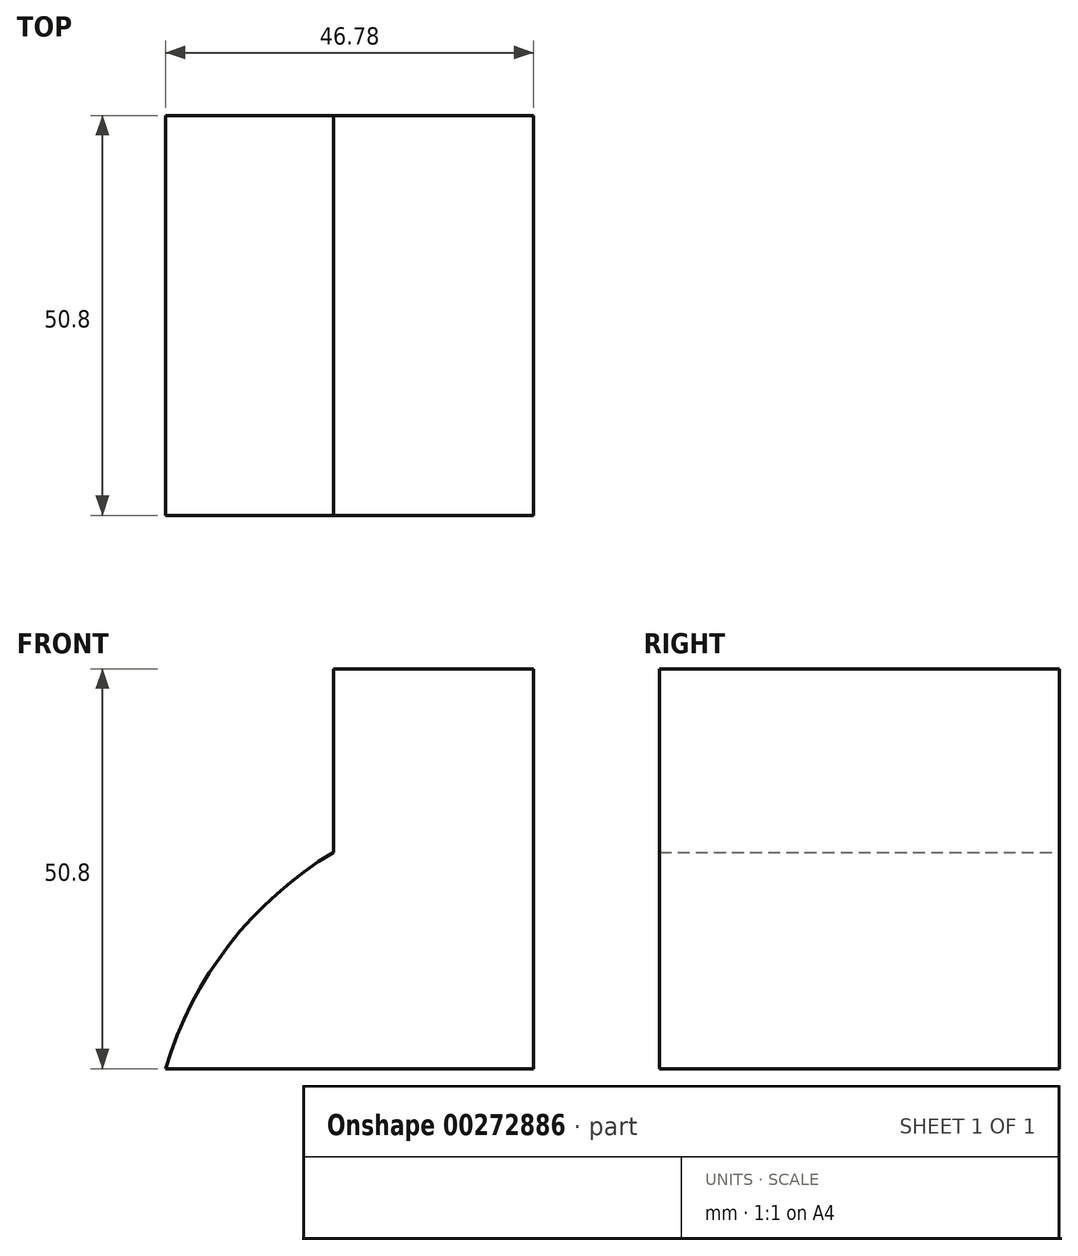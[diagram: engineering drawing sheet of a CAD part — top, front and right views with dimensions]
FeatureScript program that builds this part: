
annotation { "Feature Type Name" : "Feature", "Feature Type Description" : "" }
export const myFeature = defineFeature(function(context is Context, id is Id, definition is map)
    precondition{}
    {
        {
            var Q0;
            Q0=qCreatedBy(makeId("Front.planeOp"),FACE);
            var sketch = newSketch(context, id + "F0", { "sketchPlane" : qUnion([Q0])});
            skLineSegment(sketch, "E0", {"start": v(0, 0) * mm, "end": v(0, 50.8) * mm});
            skLineSegment(sketch, "E1", {"start": v(0, 50.8) * mm, "end": v(-25.4, 50.8) * mm});
            skLineSegment(sketch, "E2", {"start": v(-25.4, 50.8) * mm, "end": v(-25.4, 27.5) * mm});
            skArc(sketch, "E3", {"start": v(-25.4, 27.5) * mm, "mid": v(-38.67, 15.75) * mm, "end": v(-46.78, 0) * mm});
            skLineSegment(sketch, "E4", {"start": v(-46.78, 0) * mm, "end": v(0, 0) * mm});
            skSolve(sketch);
        }
        {
            var Q0;
            Q0=makeQuery(id+"F0.imprint","IMPRINT",FACE,{"disambiguationData":[TD([[makeQuery(id+"F0.imprint","IMPRINT",EDGE,{"derivedFrom":sQuery(id+"F0.wireOp",EDGE,"E0")}),1.0]])]});
            extrude(context, id + "F1", {"entities" : qUnion([Q0]), "depth" : 50.8 * mm});
        }
    });
